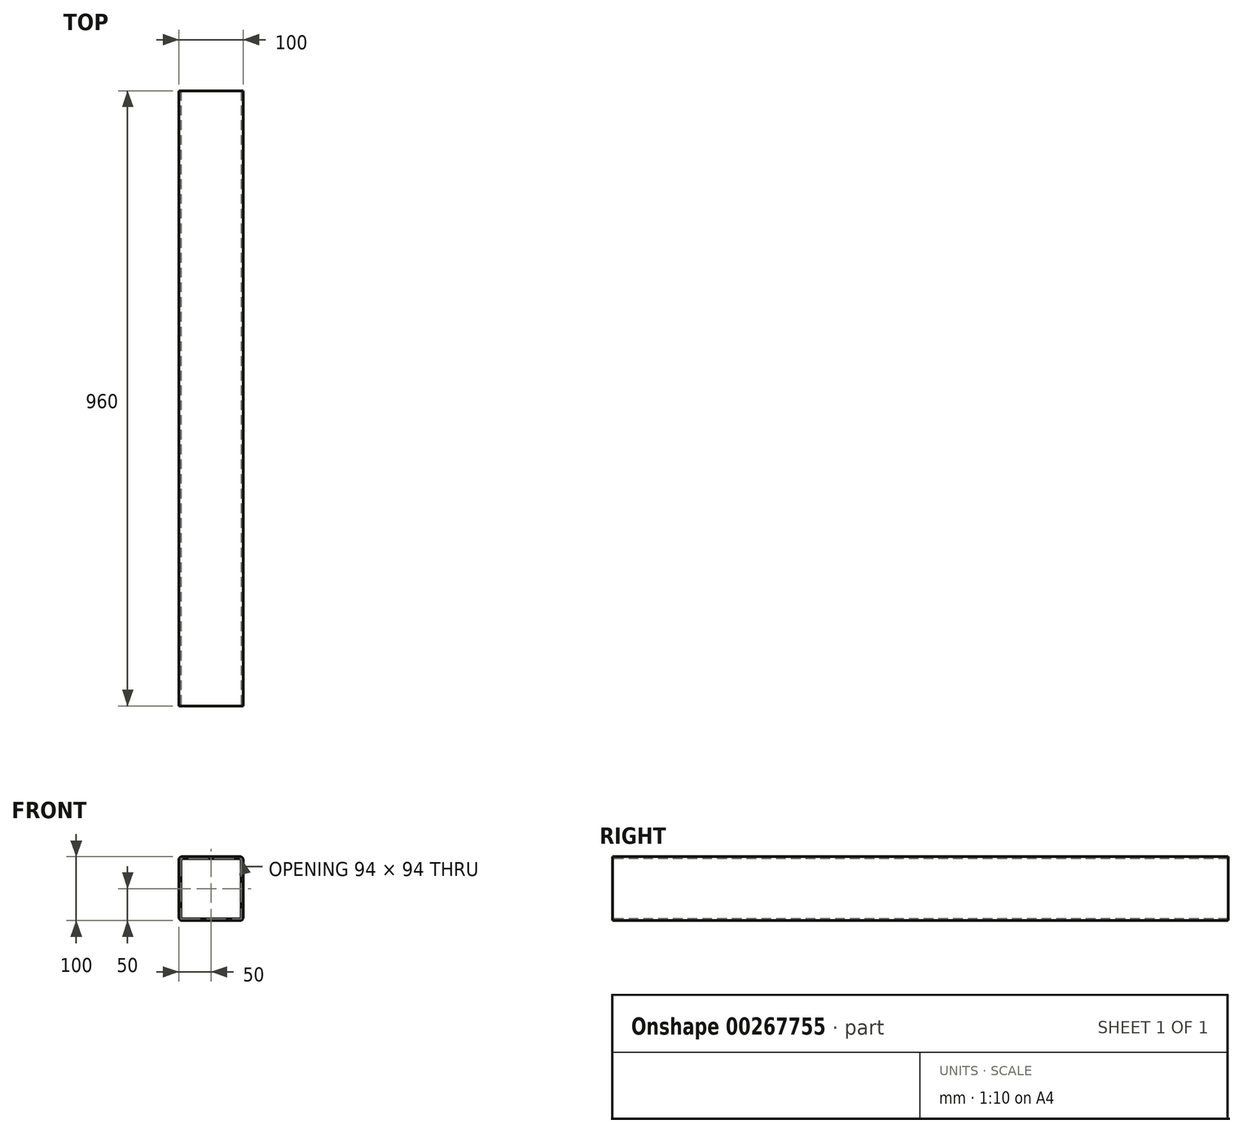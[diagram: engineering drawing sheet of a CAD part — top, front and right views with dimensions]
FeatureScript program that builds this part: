
annotation { "Feature Type Name" : "Feature", "Feature Type Description" : "" }
export const myFeature = defineFeature(function(context is Context, id is Id, definition is map)
    precondition{}
    {
        {
            var Q0;
            Q0=qCreatedBy(makeId("Front.planeOp"),FACE);
            var sketch = newSketch(context, id + "F0", { "sketchPlane" : qUnion([Q0])});
            skLineSegment(sketch, "E0.bottom", {"start": v(45, 50) * mm, "end": v(-45, 50) * mm});
            skLineSegment(sketch, "E0.top", {"start": v(45, -50) * mm, "end": v(-45, -50) * mm});
            skLineSegment(sketch, "E0.left", {"start": v(50, 45) * mm, "end": v(50, -45) * mm});
            skLineSegment(sketch, "E0.right", {"start": v(-50, 45) * mm, "end": v(-50, -45) * mm});
            skPoint(sketch, "E0.middle", {"position": v(0, 0) * mm});
            skPoint(sketch, "E1.visualSharp", {"position": v(-50, 50) * mm});
            skArc(sketch, "E1.filletArc", {"start": v(-45, 50) * mm, "mid": v(-48.54, 48.54) * mm, "end": v(-50, 45) * mm});
            skPoint(sketch, "E2.visualSharp", {"position": v(50, 50) * mm});
            skArc(sketch, "E2.filletArc", {"start": v(50, 45) * mm, "mid": v(48.54, 48.54) * mm, "end": v(45, 50) * mm});
            skPoint(sketch, "E3.visualSharp", {"position": v(50, -50) * mm});
            skArc(sketch, "E3.filletArc", {"start": v(45, -50) * mm, "mid": v(48.54, -48.54) * mm, "end": v(50, -45) * mm});
            skPoint(sketch, "E4.visualSharp", {"position": v(-50, -50) * mm});
            skArc(sketch, "E4.filletArc", {"start": v(-50, -45) * mm, "mid": v(-48.54, -48.54) * mm, "end": v(-45, -50) * mm});
            skArc(sketch, "E5.0", {"start": v(-45, 47) * mm, "mid": v(-46.41, 46.41) * mm, "end": v(-47, 45) * mm});
            skLineSegment(sketch, "E5.1", {"start": v(45, 47) * mm, "end": v(-45, 47) * mm});
            skLineSegment(sketch, "E5.2", {"start": v(-47, 45) * mm, "end": v(-47, -45) * mm});
            skArc(sketch, "E5.3", {"start": v(47, 45) * mm, "mid": v(46.41, 46.41) * mm, "end": v(45, 47) * mm});
            skArc(sketch, "E5.4", {"start": v(-47, -45) * mm, "mid": v(-46.41, -46.41) * mm, "end": v(-45, -47) * mm});
            skLineSegment(sketch, "E5.5", {"start": v(45, -47) * mm, "end": v(-45, -47) * mm});
            skArc(sketch, "E5.6", {"start": v(45, -47) * mm, "mid": v(46.41, -46.41) * mm, "end": v(47, -45) * mm});
            skLineSegment(sketch, "E5.7", {"start": v(47, 45) * mm, "end": v(47, -45) * mm});
            skSolve(sketch);
        }
        {
            var Q0;
            Q0=makeQuery(id+"F0.imprint","IMPRINT",FACE,{"disambiguationData":[TD([[makeQuery(id+"F0.imprint","IMPRINT",EDGE,{"derivedFrom":sQuery(id+"F0.wireOp",EDGE,"E0.bottom")}),1.0]])]});
            extrude(context, id + "F1", {"entities" : qUnion([Q0]), "oppositeDirection" : true, "depth" : 960 * mm});
        }
    });
